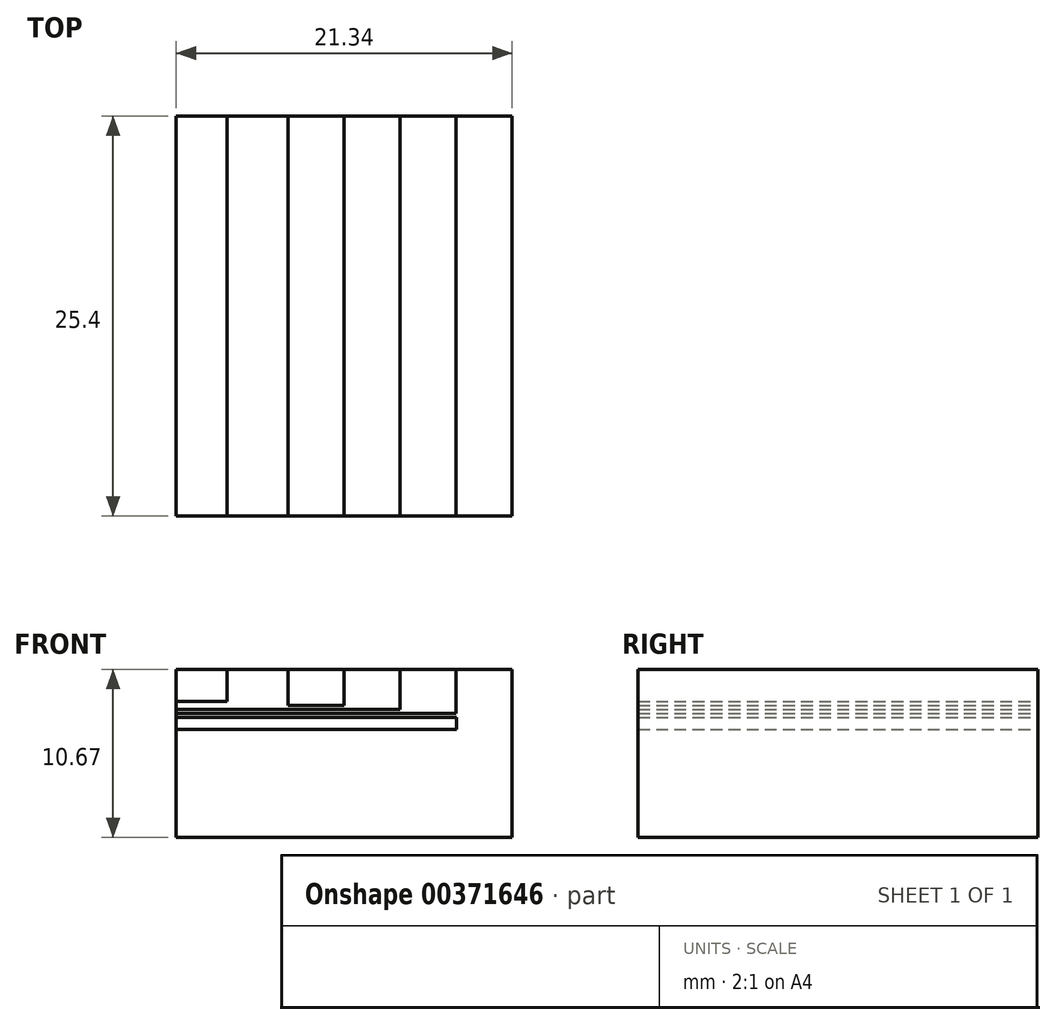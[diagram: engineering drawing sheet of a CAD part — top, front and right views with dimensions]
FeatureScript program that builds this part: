
annotation { "Feature Type Name" : "Feature", "Feature Type Description" : "" }
export const myFeature = defineFeature(function(context is Context, id is Id, definition is map)
    precondition{}
    {
        {
            var Q0;
            Q0=qCreatedBy(makeId("Front.planeOp"),FACE);
            var sketch = newSketch(context, id + "F0", { "sketchPlane" : qUnion([Q0])});
            skLineSegment(sketch, "E0.bottom", {"start": v(-77.93, 74.9) * mm, "end": v(-52.53, 74.9) * mm});
            skLineSegment(sketch, "E0.top", {"start": v(-77.93, 59.14) * mm, "end": v(-52.53, 59.14) * mm});
            skLineSegment(sketch, "E0.left", {"start": v(-77.93, 74.9) * mm, "end": v(-77.93, 59.14) * mm});
            skLineSegment(sketch, "E0.right", {"start": v(-52.53, 74.9) * mm, "end": v(-52.53, 59.14) * mm});
            skLineSegment(sketch, "E1", {"start": v(-77.93, 59.14) * mm, "end": v(-74.37, 59.14) * mm});
            skLineSegment(sketch, "E2", {"start": v(-74.37, 59.14) * mm, "end": v(-70.82, 59.14) * mm});
            skLineSegment(sketch, "E3", {"start": v(-70.82, 59.14) * mm, "end": v(-67.26, 59.14) * mm});
            skLineSegment(sketch, "E4", {"start": v(-67.26, 59.14) * mm, "end": v(-63.7, 59.14) * mm});
            skLineSegment(sketch, "E5", {"start": v(-63.7, 59.14) * mm, "end": v(-60.15, 59.14) * mm});
            skLineSegment(sketch, "E6", {"start": v(-60.15, 59.14) * mm, "end": v(-56.6, 59.14) * mm});
            skLineSegment(sketch, "E7", {"start": v(-56.6, 59.14) * mm, "end": v(-52.53, 59.14) * mm});
            skLineSegment(sketch, "E8", {"start": v(-77.93, 74.9) * mm, "end": v(-77.93, 72.86) * mm});
            skLineSegment(sketch, "E9", {"start": v(-77.93, 74.9) * mm, "end": v(-77.93, 72.6) * mm});
            skLineSegment(sketch, "E10", {"start": v(-77.93, 74.9) * mm, "end": v(-77.93, 72.35) * mm});
            skLineSegment(sketch, "E11", {"start": v(-77.93, 74.9) * mm, "end": v(-77.93, 72.1) * mm});
            skLineSegment(sketch, "E12", {"start": v(-77.93, 74.9) * mm, "end": v(-77.93, 71.84) * mm});
            skLineSegment(sketch, "E13", {"start": v(-77.93, 74.9) * mm, "end": v(-77.93, 71.08) * mm});
            skLineSegment(sketch, "E14", {"start": v(-77.93, 74.9) * mm, "end": v(-77.93, 64.22) * mm});
            skLineSegment(sketch, "E15.bottom", {"start": v(-77.93, 74.9) * mm, "end": v(-77.93, 74.9) * mm});
            skLineSegment(sketch, "E15.top", {"start": v(-77.93, 72.86) * mm, "end": v(-77.93, 72.86) * mm});
            skLineSegment(sketch, "E16.bottom", {"start": v(-77.93, 74.9) * mm, "end": v(-74.7, 74.9) * mm});
            skLineSegment(sketch, "E16.top", {"start": v(-77.93, 72.86) * mm, "end": v(-74.7, 72.86) * mm});
            skLineSegment(sketch, "E16.right", {"start": v(-74.7, 74.9) * mm, "end": v(-74.7, 72.86) * mm});
            skLineSegment(sketch, "E17.bottom", {"start": v(-77.93, 74.9) * mm, "end": v(-70.82, 74.9) * mm});
            skLineSegment(sketch, "E17.top", {"start": v(-77.93, 72.6) * mm, "end": v(-70.82, 72.6) * mm});
            skLineSegment(sketch, "E17.right", {"start": v(-70.82, 74.9) * mm, "end": v(-70.82, 72.6) * mm});
            skLineSegment(sketch, "E18.bottom", {"start": v(-70.82, 74.9) * mm, "end": v(-70.82, 74.9) * mm});
            skLineSegment(sketch, "E18.top", {"start": v(-70.82, 72.6) * mm, "end": v(-70.82, 72.6) * mm});
            skLineSegment(sketch, "E19.bottom", {"start": v(-70.82, 74.9) * mm, "end": v(-67.26, 74.9) * mm});
            skLineSegment(sketch, "E19.top", {"start": v(-70.82, 72.6) * mm, "end": v(-67.26, 72.6) * mm});
            skLineSegment(sketch, "E19.right", {"start": v(-67.26, 74.9) * mm, "end": v(-67.26, 72.6) * mm});
            skLineSegment(sketch, "E20.bottom", {"start": v(-77.93, 74.9) * mm, "end": v(-63.7, 74.9) * mm});
            skLineSegment(sketch, "E20.top", {"start": v(-77.93, 72.35) * mm, "end": v(-63.7, 72.35) * mm});
            skLineSegment(sketch, "E20.right", {"start": v(-63.7, 74.9) * mm, "end": v(-63.7, 72.35) * mm});
            skLineSegment(sketch, "E21.bottom", {"start": v(-77.93, 74.9) * mm, "end": v(-60.15, 74.9) * mm});
            skLineSegment(sketch, "E21.top", {"start": v(-77.93, 72.1) * mm, "end": v(-60.15, 72.1) * mm});
            skLineSegment(sketch, "E21.right", {"start": v(-60.15, 74.9) * mm, "end": v(-60.15, 72.1) * mm});
            skLineSegment(sketch, "E22.bottom", {"start": v(-77.93, 71.84) * mm, "end": v(-77.93, 71.84) * mm});
            skLineSegment(sketch, "E22.top", {"start": v(-77.93, 71.08) * mm, "end": v(-77.93, 71.08) * mm});
            skLineSegment(sketch, "E22.left", {"start": v(-77.93, 71.84) * mm, "end": v(-77.93, 71.08) * mm});
            skLineSegment(sketch, "E22.right", {"start": v(-77.93, 71.84) * mm, "end": v(-77.93, 71.08) * mm});
            skLineSegment(sketch, "E23.bottom", {"start": v(-60.11, 71.84) * mm, "end": v(-77.93, 71.84) * mm});
            skLineSegment(sketch, "E23.top", {"start": v(-60.11, 71.08) * mm, "end": v(-77.93, 71.08) * mm});
            skLineSegment(sketch, "E23.left", {"start": v(-60.11, 71.84) * mm, "end": v(-60.11, 71.08) * mm});
            skLineSegment(sketch, "E24.bottom", {"start": v(-77.93, 74.9) * mm, "end": v(-56.6, 74.9) * mm});
            skLineSegment(sketch, "E24.top", {"start": v(-77.93, 64.22) * mm, "end": v(-56.6, 64.22) * mm});
            skLineSegment(sketch, "E24.right", {"start": v(-56.6, 74.9) * mm, "end": v(-56.6, 64.22) * mm});
            skSolve(sketch);
        }
        {
            var Q0;
            {var subQ0=sQuery(id+"F0.wireOp",EDGE,"E16.top");Q0=makeQuery(id+"F0.imprint","IMPRINT",FACE,{"disambiguationData":[TD([[makeQuery(id+"F0.imprint","IMPRINT",EDGE,{"derivedFrom":subQ0}),1.0]])]});}
            var Q1;
            Q1=makeQuery(id+"F0.imprint","IMPRINT",FACE,{"disambiguationData":[TD([[makeQuery(id+"F0.imprint","IMPRINT",EDGE,{"derivedFrom":sQuery(id+"F0.wireOp",EDGE,"E19.top")}),1.0]])]});
            var Q2;
            {var subQ3=sQuery(id+"F0.wireOp",EDGE,"E20.top");Q2=makeQuery(id+"F0.imprint","IMPRINT",FACE,{"disambiguationData":[TD([[makeQuery(id+"F0.imprint","IMPRINT",EDGE,{"derivedFrom":subQ3}),-1.0]])]});}
            var Q3;
            {var subQ0=sQuery(id+"F0.wireOp",EDGE,"E23.bottom");Q3=makeQuery(id+"F0.imprint","IMPRINT",FACE,{"disambiguationData":[TD([[makeQuery(id+"F0.imprint","IMPRINT",EDGE,{"derivedFrom":subQ0}),1.0]])]});}
            var Q4;
            Q4=makeQuery(id+"F0.imprint","IMPRINT",FACE,{"disambiguationData":[TD([[makeQuery(id+"F0.imprint","IMPRINT",EDGE,{"derivedFrom":sQuery(id+"F0.wireOp",EDGE,"E0.bottom")}),-1.0]])]});
            extrude(context, id + "F1", {"entities" : qUnion([Q0, Q1, Q2, Q3, Q4]), "depth" : 25.4 * mm});
        }
        {
            var Q0;
            {var subQ3=sQuery(id+"F0.wireOp",EDGE,"E16.top");Q0=makeQuery(id+"F0.imprint","IMPRINT",FACE,{"disambiguationData":[TD([[makeQuery(id+"F0.imprint","IMPRINT",EDGE,{"derivedFrom":subQ3}),-1.0]])]});}
            var Q1;
            {var subQ4=sQuery(id+"F0.wireOp",EDGE,"E17.top");Q1=makeQuery(id+"F0.imprint","IMPRINT",FACE,{"disambiguationData":[TD([[makeQuery(id+"F0.imprint","IMPRINT",EDGE,{"derivedFrom":subQ4}),-1.0]])]});}
            extrude(context, id + "F2", {"entities" : qUnion([Q0, Q1]), "depth" : 25.4 * mm});
        }
        {
            var Q0;
            {var subQ3=sQuery(id+"F0.wireOp",EDGE,"E21.top");Q0=makeQuery(id+"F0.imprint","IMPRINT",FACE,{"disambiguationData":[TD([[makeQuery(id+"F0.imprint","IMPRINT",EDGE,{"derivedFrom":subQ3}),-1.0]])]});}
            extrude(context, id + "F3", {"entities" : qUnion([Q0]), "depth" : 25.4 * mm});
        }
    });
